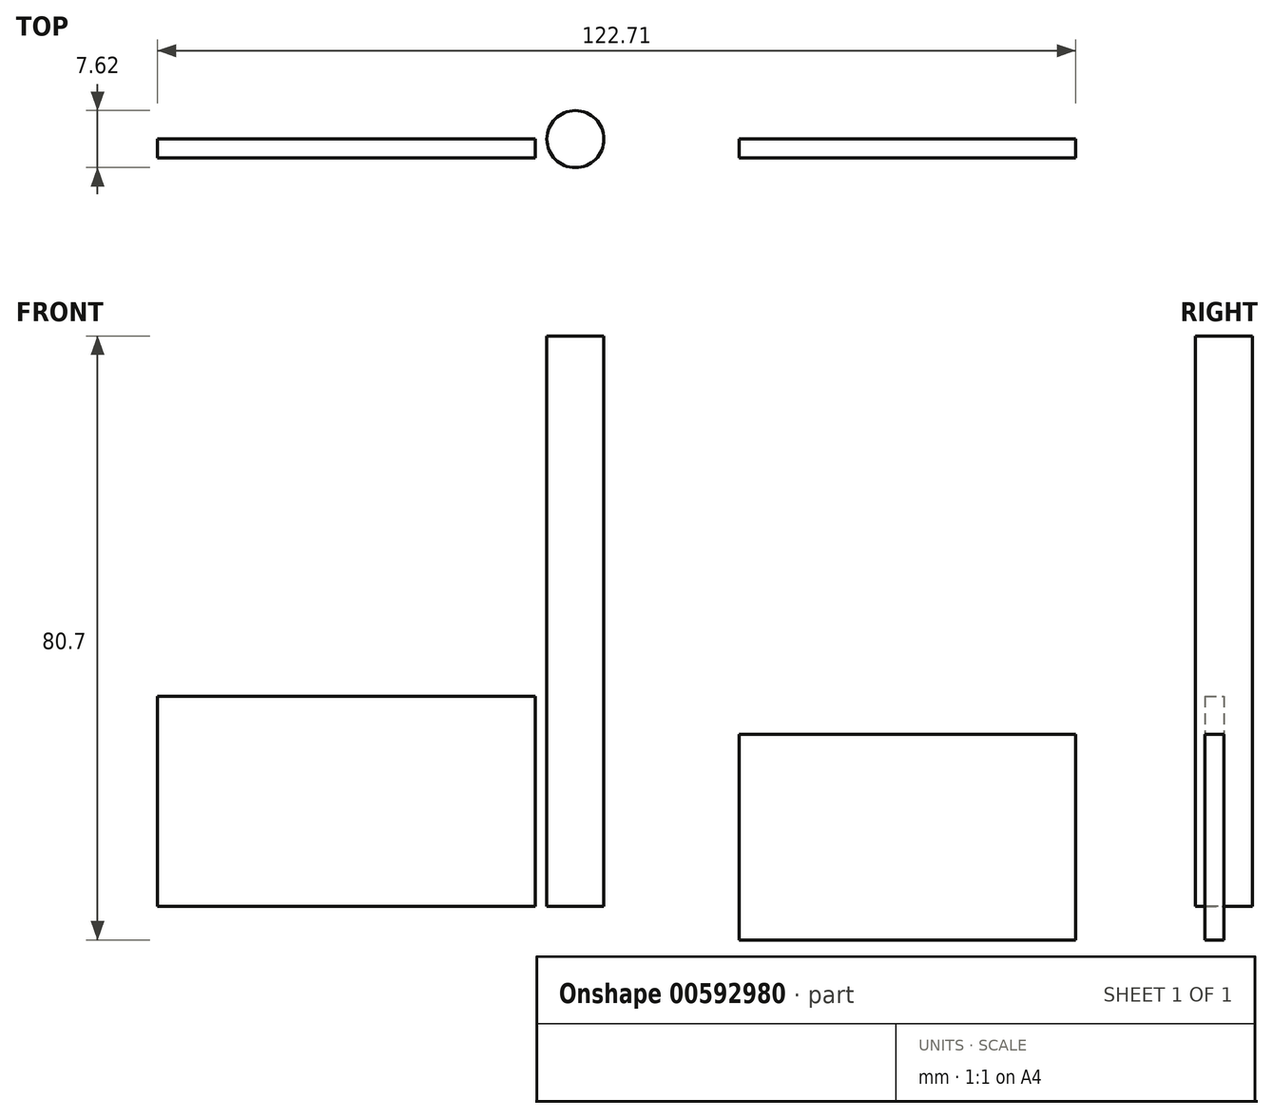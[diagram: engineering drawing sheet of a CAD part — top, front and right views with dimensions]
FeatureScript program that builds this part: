
annotation { "Feature Type Name" : "Feature", "Feature Type Description" : "" }
export const myFeature = defineFeature(function(context is Context, id is Id, definition is map)
    precondition{}
    {
        {
            var Q0;
            Q0=qCreatedBy(makeId("Front.planeOp"),FACE);
            var sketch = newSketch(context, id + "F0", { "sketchPlane" : qUnion([Q0])});
            skLineSegment(sketch, "E0.bottom", {"start": v(-55.85, 28.07) * mm, "end": v(-5.34, 28.07) * mm});
            skLineSegment(sketch, "E0.top", {"start": v(-55.85, 0) * mm, "end": v(-5.34, 0) * mm});
            skLineSegment(sketch, "E0.left", {"start": v(-55.85, 28.07) * mm, "end": v(-55.85, 0) * mm});
            skLineSegment(sketch, "E0.right", {"start": v(-5.34, 28.07) * mm, "end": v(-5.34, 0) * mm});
            skSolve(sketch);
        }
        {
            var Q0;
            Q0 = qSketchRegion(id + "F0", true);
            extrude(context, id + "F1", {"entities" : qUnion([Q0]), "depth" : 2.54 * mm, "offsetDistance" : 25.4 * mm});
        }
        {
            var Q0;
            Q0=qCreatedBy(makeId("Front.planeOp"),FACE);
            var sketch = newSketch(context, id + "F2", { "sketchPlane" : qUnion([Q0])});
            skLineSegment(sketch, "E1.bottom", {"start": v(21.86, 22.98) * mm, "end": v(66.86, 22.98) * mm});
            skLineSegment(sketch, "E1.top", {"start": v(21.86, -4.5) * mm, "end": v(66.86, -4.5) * mm});
            skLineSegment(sketch, "E1.left", {"start": v(21.86, 22.98) * mm, "end": v(21.86, -4.5) * mm});
            skLineSegment(sketch, "E1.right", {"start": v(66.86, 22.98) * mm, "end": v(66.86, -4.5) * mm});
            skSolve(sketch);
        }
        {
            var Q0;
            Q0 = qSketchRegion(id + "F2", true);
            extrude(context, id + "F3", {"entities" : qUnion([Q0]), "depth" : 2.54 * mm, "offsetDistance" : 25.4 * mm});
        }
        {
            var Q0;
            Q0=qCreatedBy(makeId("Top.planeOp"),FACE);
            var sketch = newSketch(context, id + "F4", { "sketchPlane" : qUnion([Q0])});
            skCircle(sketch, "E2", {"center": v(0, 0) * mm, "radius": 3.81 * mm});
            skSolve(sketch);
        }
        {
            var Q0;
            Q0 = qSketchRegion(id + "F4", true);
            extrude(context, id + "F5", {"entities" : qUnion([Q0]), "depth" : 76.2 * mm, "offsetDistance" : 25.4 * mm});
        }
    });
